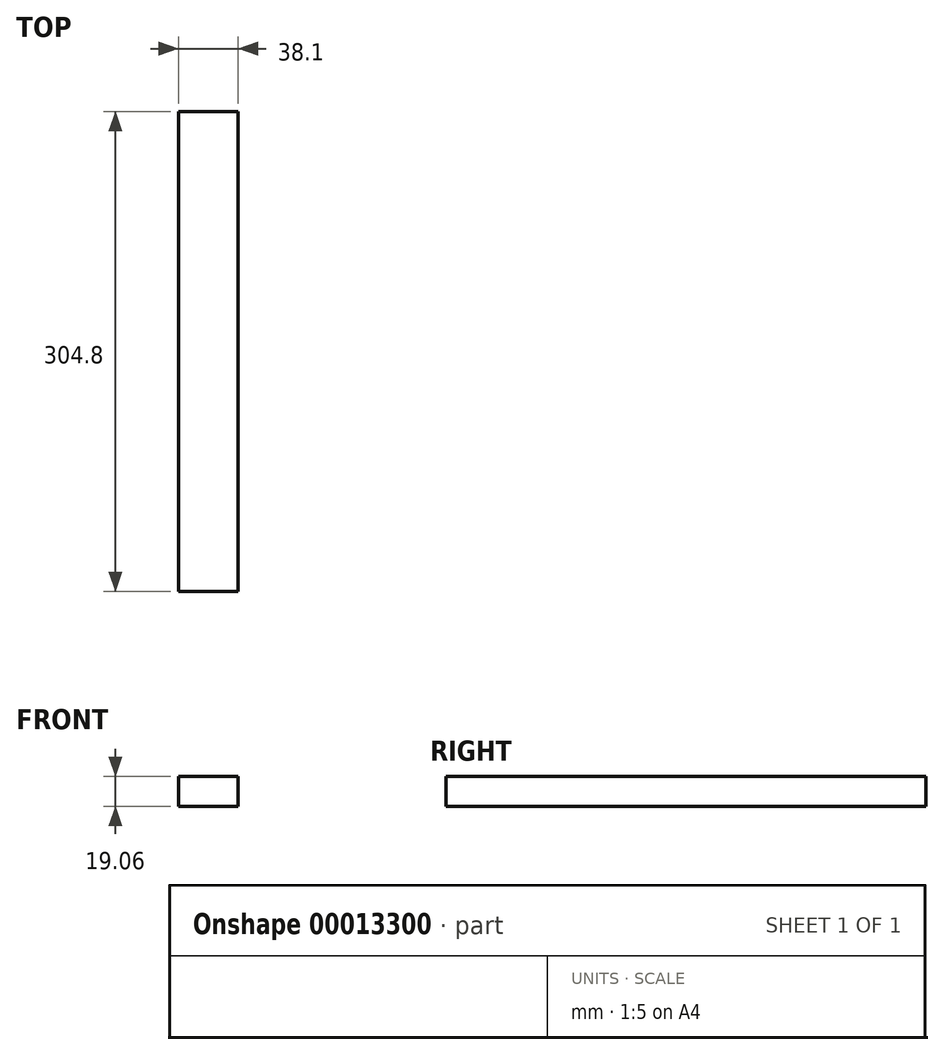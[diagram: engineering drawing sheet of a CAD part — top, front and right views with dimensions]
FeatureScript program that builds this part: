
annotation { "Feature Type Name" : "Feature", "Feature Type Description" : "" }
export const myFeature = defineFeature(function(context is Context, id is Id, definition is map)
    precondition{}
    {
        {
            var Q0;
            Q0=qCreatedBy(makeId("Front.planeOp"),FACE);
            var sketch = newSketch(context, id + "F0", { "sketchPlane" : qUnion([Q0])});
            skLineSegment(sketch, "E0.rect.bottom", {"start": v(19.05, 9.53) * mm, "end": v(-19.05, 9.53) * mm});
            skLineSegment(sketch, "E0.rect.top", {"start": v(19.05, -9.53) * mm, "end": v(-19.05, -9.53) * mm});
            skLineSegment(sketch, "E0.rect.left", {"start": v(19.05, 9.53) * mm, "end": v(19.05, -9.53) * mm});
            skLineSegment(sketch, "E0.rect.right", {"start": v(-19.05, 9.53) * mm, "end": v(-19.05, -9.53) * mm});
            skPoint(sketch, "E0.rect.middle", {"position": v(0, 0) * mm});
            skSolve(sketch);
        }
        {
            var Q0;
            Q0=makeQuery(id+"F0.imprint","IMPRINT",FACE,{"disambiguationData":[TD([[makeQuery(id+"F0.imprint","IMPRINT",EDGE,{"derivedFrom":sQuery(id+"F0.wireOp",EDGE,"E0.rect.bottom")}),1.0]])]});
            extrude(context, id + "F1", {"entities" : qUnion([Q0]), "endBound" : BoundingType.SYMMETRIC, "depth" : 304.8 * mm});
        }
    });
